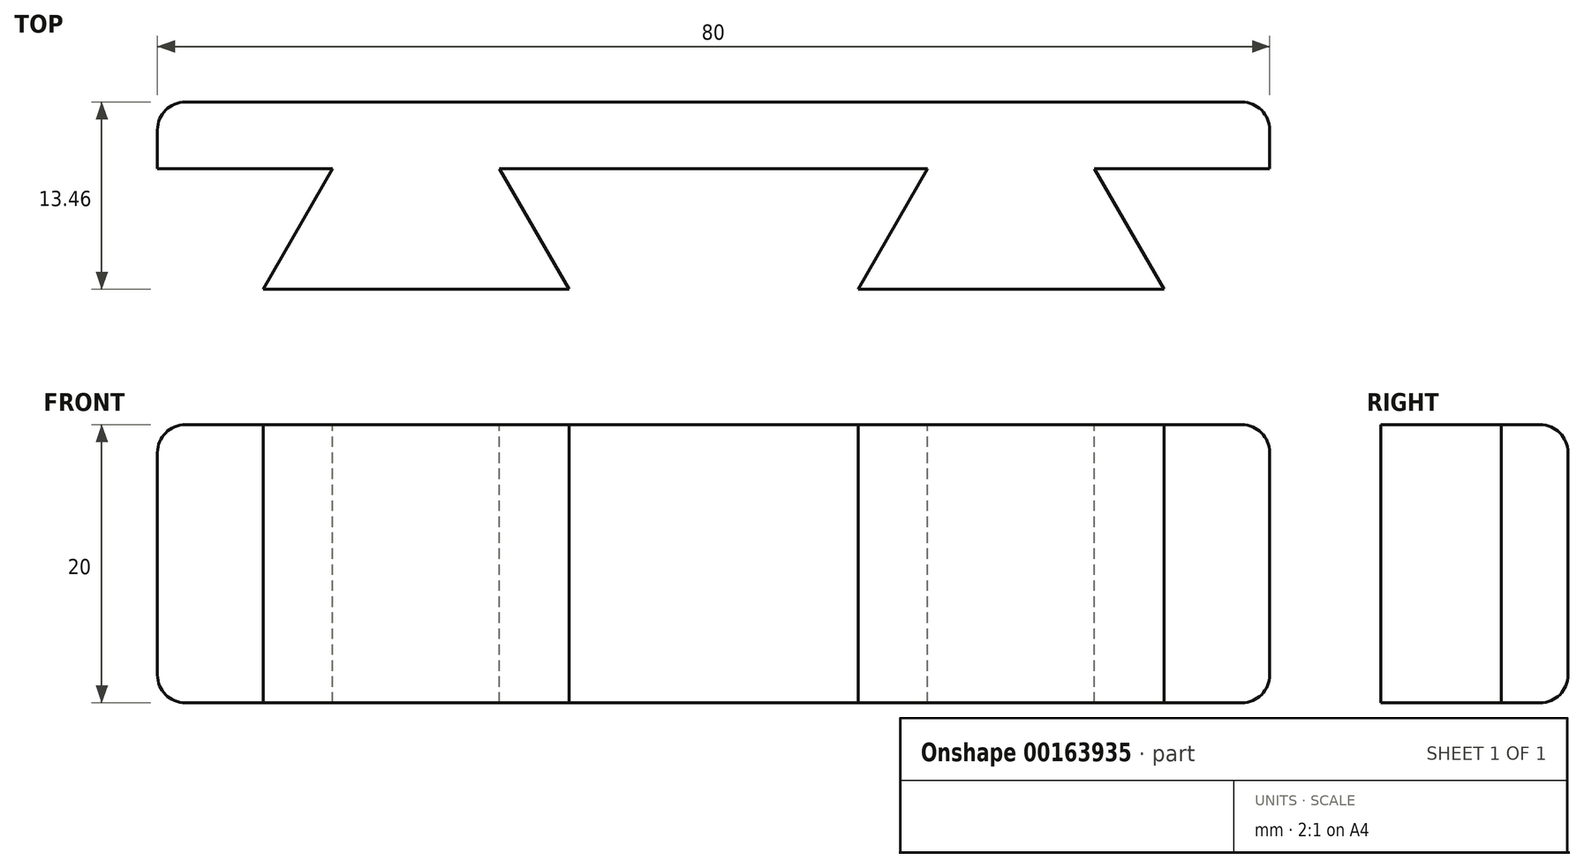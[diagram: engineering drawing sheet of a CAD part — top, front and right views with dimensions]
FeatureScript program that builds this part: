
annotation { "Feature Type Name" : "Feature", "Feature Type Description" : "" }
export const myFeature = defineFeature(function(context is Context, id is Id, definition is map)
    precondition{}
    {
        {
            var Q0;
            Q0=qCreatedBy(makeId("Top.planeOp"),FACE);
            var sketch = newSketch(context, id + "F0", { "sketchPlane" : qUnion([Q0])});
            skLineSegment(sketch, "E0", {"start": v(-40, 15) * mm, "end": v(-27.4, 15) * mm});
            skLineSegment(sketch, "E1", {"start": v(-27.4, 15) * mm, "end": v(-32.4, 6.34) * mm});
            skLineSegment(sketch, "E2", {"start": v(-32.4, 6.34) * mm, "end": v(-10.4, 6.34) * mm});
            skLineSegment(sketch, "E3", {"start": v(-10.4, 6.34) * mm, "end": v(-15.4, 15) * mm});
            skLineSegment(sketch, "E4", {"start": v(-15.4, 15) * mm, "end": v(0, 15) * mm});
            skLineSegment(sketch, "E5", {"start": v(-27.4, 15) * mm, "end": v(-15.4, 15) * mm});
            skLineSegment(sketch, "E6.MirrorCS", {"start": v(-40, 30) * mm, "end": v(-40, 15) * mm});
            skLineSegment(sketch, "E7.MirrorCS", {"start": v(0, 30) * mm, "end": v(-40, 30) * mm});
            skLineSegment(sketch, "E8", {"start": v(0, 30) * mm, "end": v(0, 26.65) * mm});
            skLineSegment(sketch, "E9.MirrorCS", {"start": v(0, 30) * mm, "end": v(40, 30) * mm});
            skLineSegment(sketch, "E10.MirrorCS", {"start": v(40, 30) * mm, "end": v(40, 15) * mm});
            skLineSegment(sketch, "E11.MirrorCS", {"start": v(40, 15) * mm, "end": v(27.4, 15) * mm});
            skLineSegment(sketch, "E12.MirrorCS", {"start": v(27.4, 15) * mm, "end": v(32.4, 6.34) * mm});
            skLineSegment(sketch, "E13.MirrorCS", {"start": v(32.4, 6.34) * mm, "end": v(10.4, 6.34) * mm});
            skLineSegment(sketch, "E14.MirrorCS", {"start": v(10.4, 6.34) * mm, "end": v(15.4, 15) * mm});
            skLineSegment(sketch, "E15.MirrorCS", {"start": v(15.4, 15) * mm, "end": v(0, 15) * mm});
            skLineSegment(sketch, "E16", {"start": v(-40, 15) * mm, "end": v(-40, 19.8) * mm});
            skLineSegment(sketch, "E17", {"start": v(-40, 19.8) * mm, "end": v(40, 19.8) * mm});
            skSolve(sketch);
        }
        {
            var Q0;
            Q0=makeQuery(id+"F0.imprint","IMPRINT",FACE,{"disambiguationData":[TD([[makeQuery(id+"F0.imprint","IMPRINT",EDGE,{"derivedFrom":sQuery(id+"F0.wireOp",EDGE,"E1")}),1.0]])]});
            var Q1;
            {var subQ3=sQuery(id+"F0.wireOp",EDGE,"E0");Q1=makeQuery(id+"F0.imprint","IMPRINT",FACE,{"disambiguationData":[TD([[makeQuery(id+"F0.imprint","IMPRINT",EDGE,{"derivedFrom":subQ3}),1.0]])]});}
            extrude(context, id + "F1", {"entities" : qUnion([Q0, Q1]), "oppositeDirection" : true, "depth" : 20 * mm});
        }
        {
            var Q0;
            Q0=makeQuery(id+"F1.opExtrude","SWEPT_FACE",FACE,{"disambiguationData":[OSD([sQuery(id+"F0.wireOp",EDGE,"E17")])]});
            var Q1;
            Q1=makeQuery(id+"F1.opExtrude","CAP_EDGE",EDGE,{"disambiguationData":[OSD([sQuery(id+"F0.wireOp",EDGE,"E10.MirrorCS")])],"isStart":true});
            var Q2;
            Q2=makeQuery(id+"F1.opExtrude","CAP_EDGE",EDGE,{"disambiguationData":[OSD([sQuery(id+"F0.wireOp",EDGE,"E10.MirrorCS")])],"isStart":false});
            var Q3;
            Q3=makeQuery(id+"F1.opExtrude","CAP_EDGE",EDGE,{"disambiguationData":[OSD([sQuery(id+"F0.wireOp",EDGE,"E6.MirrorCS")])],"isStart":true});
            var Q4;
            Q4=makeQuery(id+"F1.opExtrude","CAP_EDGE",EDGE,{"disambiguationData":[OSD([sQuery(id+"F0.wireOp",EDGE,"E6.MirrorCS")])],"isStart":false});
            fillet(context, id + "F2", {"entities" : qUnion([Q0, Q1, Q2, Q3, Q4]), "radius" : 2 * mm, "tangentPropagation" : true, "allowEdgeOverflow" : false});
        }
    });
